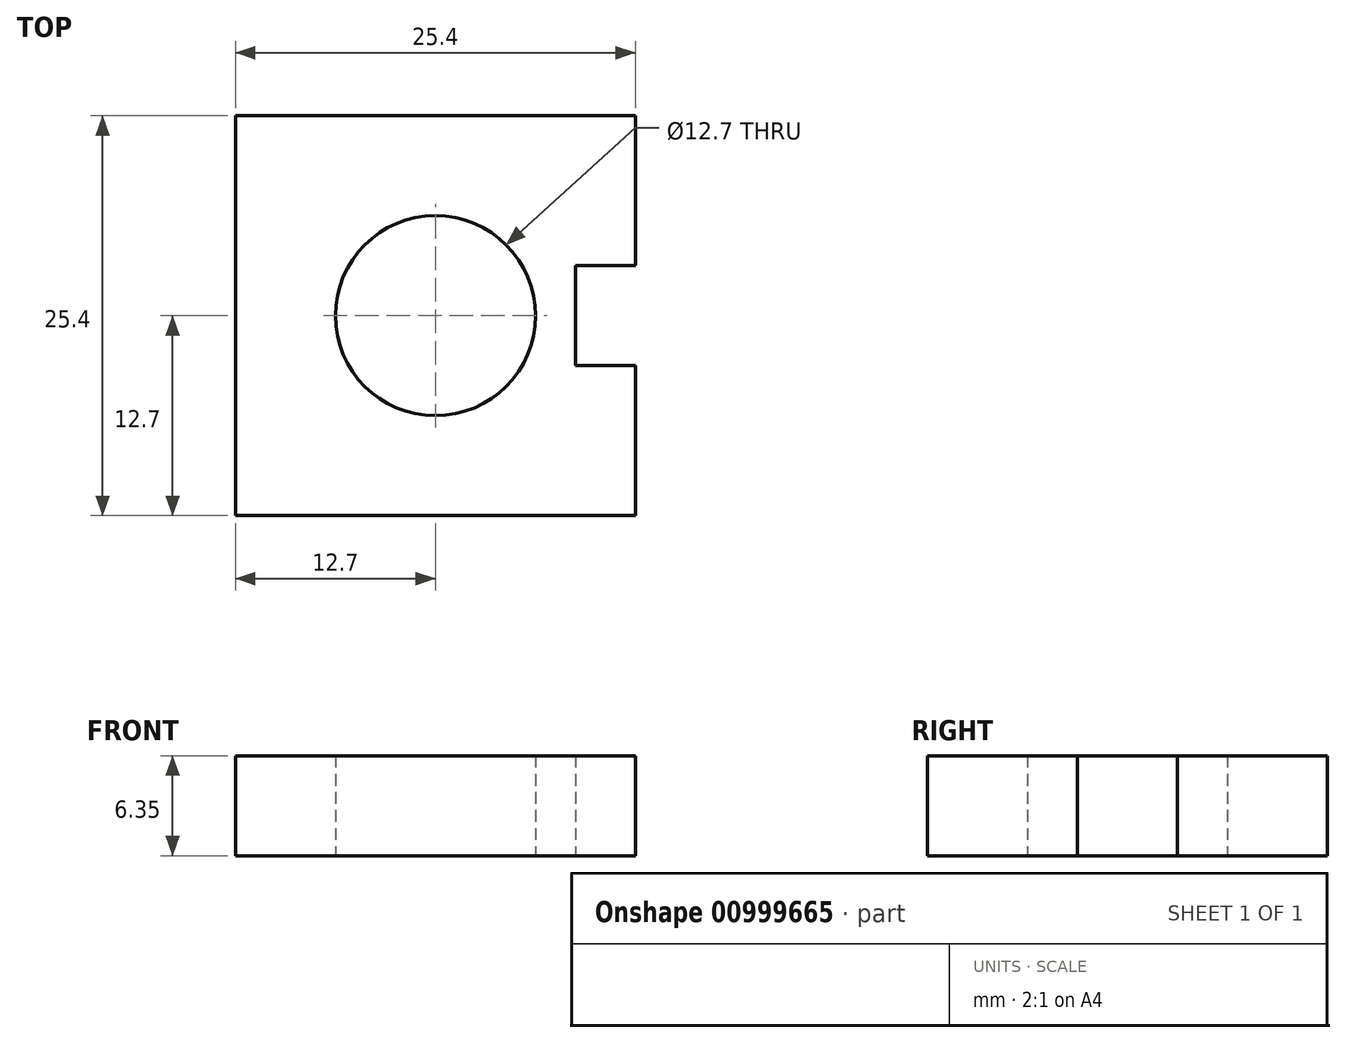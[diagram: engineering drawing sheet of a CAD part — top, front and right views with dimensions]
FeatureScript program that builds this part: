
annotation { "Feature Type Name" : "Feature", "Feature Type Description" : "" }
export const myFeature = defineFeature(function(context is Context, id is Id, definition is map)
    precondition{}
    {
        {
            var Q0;
            Q0=qCreatedBy(makeId("Top.planeOp"),FACE);
            var sketch = newSketch(context, id + "F0", { "sketchPlane" : qUnion([Q0])});
            skLineSegment(sketch, "E0.bottom", {"start": v(0, 0) * mm, "end": v(25.4, 0) * mm});
            skLineSegment(sketch, "E0.top", {"start": v(0, 25.4) * mm, "end": v(25.4, 25.4) * mm});
            skLineSegment(sketch, "E0.left", {"start": v(0, 0) * mm, "end": v(0, 25.4) * mm});
            skLineSegment(sketch, "E0.right", {"start": v(25.4, 0) * mm, "end": v(25.4, 9.53) * mm});
            skCircle(sketch, "E1", {"center": v(12.7, 12.7) * mm, "radius": 6.35 * mm});
            skPoint(sketch, "E1.centerSnap0", {"position": v(12.7, 25.4) * mm});
            skPoint(sketch, "E1.centerSnap1", {"position": v(0, 12.7) * mm});
            skLineSegment(sketch, "E2.bottom", {"start": v(25.4, 15.88) * mm, "end": v(21.59, 15.88) * mm});
            skLineSegment(sketch, "E2.top", {"start": v(25.4, 9.53) * mm, "end": v(21.59, 9.53) * mm});
            skLineSegment(sketch, "E2.right", {"start": v(21.59, 15.88) * mm, "end": v(21.59, 9.53) * mm});
            skLineSegment(sketch, "E3.trimOffspring", {"start": v(25.4, 15.88) * mm, "end": v(25.4, 25.4) * mm});
            skSolve(sketch);
        }
        {
            var Q0;
            Q0 = qSketchRegion(id + "F0", true);
            extrude(context, id + "F1", {"entities" : qUnion([Q0]), "depth" : 6.35 * mm, "offsetDistance" : 25.4 * mm});
        }
    });
